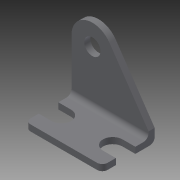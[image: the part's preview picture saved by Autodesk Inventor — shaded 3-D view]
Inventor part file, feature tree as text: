
AUTODESK INVENTOR PART (.ipt)
format: ipt  version: 2014 (Build 180170000, 170)  size: 187,392 bytes
history: native  units: in
note: dims shown in document units (in); Inventor stores cm internally (conversion verified against a paired STEP export)
features: other x161, sketch x8, extrude x5, hole x3
ambient origin geometry x8: Origin, YZ Plane, XZ Plane, XY Plane, X Axis, Y Axis, Z Axis, Center Point
bodies: Solid1 (feature_tree)
feature tree (177):
  extrude  "Extrusion1"  Depth=0.51in TaperAngle=0.0deg
  extrude  "Extrusion2"  Depth=0.0598in TaperAngle=0.0deg
  hole  "Hole1"  [1 undecoded]
  hole  "Hole2"  [1 undecoded]
  hole  "Hole3"  [1 undecoded]
  sketch  "Sketch_6"
  sketch  "Sketch_7"
  extrude  "Extrusion3"  [1 undecoded]
  extrude  "Extrusion4"  [1 undecoded]
  extrude  "Extrusion5"  [1 undecoded]
  other  "a1_XY"
  other  "a1_YZ"
  other  "a1_ZX"
  other  "a1_X"
  other  "a1_Y"
  other  "a1_Z"
  other  "a1_Center"
  other  "a2_XY"
  other  "a2_YZ"
  other  "a2_ZX"
  other  "a2_X"
  other  "a2_Y"
  other  "a2_Z"
  other  "a2_Center"
  other  "b1_XY"
  other  "b1_YZ"
  other  "b1_ZX"
  other  "b1_X"
  other  "b1_Y"
  other  "b1_Z"
  other  "b1_Center"
  other  "b2_XY"
  other  "b2_YZ"
  other  "b2_ZX"
  other  "b2_X"
  other  "b2_Y"
  other  "b2_Z"
  other  "b2_Center"
  other  "c1_XY"
  other  "c1_YZ"
  other  "c1_ZX"
  other  "c1_X"
  other  "c1_Y"
  other  "c1_Z"
  other  "c1_Center"
  other  "d1_XY"
  other  "d1_YZ"
  other  "d1_ZX"
  other  "d1_X"
  other  "d1_Y"
  other  "d1_Z"
  other  "d1_Center"
  other  "d2_XY"
  other  "d2_YZ"
  other  "d2_ZX"
  other  "d2_X"
  other  "d2_Y"
  other  "d2_Z"
  other  "d2_Center"
  other  "e1_XY"
  other  "e1_YZ"
  other  "e1_ZX"
  other  "e1_X"
  other  "e1_Y"
  other  "e1_Z"
  other  "e1_Center"
  other  "e2_XY"
  other  "e2_YZ"
  other  "e2_ZX"
  other  "e2_X"
  other  "e2_Y"
  other  "e2_Z"
  other  "e2_Center"
  other  "f1_XY"
  other  "f1_YZ"
  other  "f1_ZX"
  other  "f1_X"
  other  "f1_Y"
  other  "f1_Z"
  other  "f1_Center"
  other  "f2_XY"
  other  "f2_YZ"
  other  "f2_ZX"
  other  "f2_X"
  other  "f2_Y"
  other  "f2_Z"
  other  "f2_Center"
  other  "g1_XY"
  other  "g1_YZ"
  other  "g1_ZX"
  other  "g1_X"
  other  "g1_Y"
  other  "g1_Z"
  other  "g1_Center"
  other  "g2_XY"
  other  "g2_YZ"
  other  "g2_ZX"
  other  "g2_X"
  other  "g2_Y"
  other  "g2_Z"
  other  "g2_Center"
  other  "h1_XY"
  other  "h1_YZ"
  other  "h1_ZX"
  other  "h1_X"
  other  "h1_Y"
  other  "h1_Z"
  other  "h1_Center"
  other  "h2_XY"
  other  "h2_YZ"
  other  "h2_ZX"
  other  "h2_X"
  other  "h2_Y"
  other  "h2_Z"
  other  "h2_Center"
  other  "i_XY"
  other  "i_YZ"
  other  "i_ZX"
  other  "i_X"
  other  "i_Y"
  other  "i_Z"
  other  "i_Center"
  other  "j1_XY"
  other  "j1_YZ"
  other  "j1_ZX"
  other  "j1_X"
  other  "j1_Y"
  other  "j1_Z"
  other  "j1_Center"
  other  "j2_XY"
  other  "j2_YZ"
  other  "j2_ZX"
  other  "j2_X"
  other  "j2_Y"
  other  "j2_Z"
  other  "j2_Center"
  other  "k1_XY"
  other  "k1_YZ"
  other  "k1_ZX"
  other  "k1_X"
  other  "k1_Y"
  other  "k1_Z"
  other  "k1_Center"
  other  "k11_XY"
  other  "k11_YZ"
  other  "k11_ZX"
  other  "k11_X"
  other  "k11_Y"
  other  "k11_Z"
  other  "k11_Center"
  other  "k12_XY"
  other  "k12_YZ"
  other  "k12_ZX"
  other  "k12_X"
  other  "k12_Y"
  other  "k12_Z"
  other  "k12_Center"
  other  "to_dummy_L_XY"
  other  "to_dummy_L_YZ"
  other  "to_dummy_L_ZX"
  other  "to_dummy_L_X"
  other  "to_dummy_L_Y"
  other  "to_dummy_L_Z"
  other  "to_dummy_L_Center"
  other  "to_pin_L_XY"
  other  "to_pin_L_YZ"
  other  "to_pin_L_ZX"
  other  "to_pin_L_X"
  other  "to_pin_L_Y"
  other  "to_pin_L_Z"
  other  "to_pin_L_Center"
  sketch  "Sketch_1"  dims[d0=0.75in d1=0.0in d2=0.51in d3=0.0in]
  sketch  "Sketch_2"  dims[d4=0.1585in d5=0.75in d6=0.375in d7=0.25in d8=0.5635in d9=0.0598in d10=0.0in]
  sketch  "Sketch3"  dims[d11=0.19in d12=0.75in d13=0.375in d14=0.25in d15=0.5635in d16=0.0598in d17=0.0in]
  sketch  "Sketch4"  dims[d18=0.19in d19=0.75in d20=0.375in d21=0.25in d22=0.5635in d23=0.0598in d24=0.0in d25=0.0598in d26=0.0in]
  sketch  "Sketch5"  dims[d27=0.0598in d28=0.0in d29=0.0598in d30=0.0in]
  sketch  "Sketch_8"
note: 6 required parameter values undecoded (feature->parameter linkage not recoverable at this tier; creation-order binding heuristic only, values carry confidence <= 0.55)
